# Revit family: METALFIRE_ULTIME_D_MF_WHE_2S
name_source: partatom
category: Mechanical Equipment
revit_build: Autodesk Revit 2018 (Build: 20190510_1515(x64)
units: mm (PartAtom-declared; Revit-internal decimal feet)

## family parameters
Always vertical = Yes
Cut with Voids When Loaded = No
Host = Wall
OmniClass Number = 23.75.00.00
OmniClass Title = Climate Control (HVAC)
Part Type = Normal
Room Calculation Point = Yes
Round Connector Dimension = Use Diameter
Shared = No

## types (1)
- METALFIRE_ULTIME_D_MF_WHE_2S
    BIM BADGE = https://bim.archiproducts.com
    CO EMISSION = 0.07%
    DEPTH = 401 mm
    Description = This generation of room air independent wood fireplaces with liftable door is equipped with a dynamic combustion technique that ensures optimal combustion and high efficiency.
    ENERGY EFFICIENCY CLASS = A+
    FINE DUST EMISSION = 30 mg/Nm3
    FINISHING MATERIAL = Painted steel, cast iron
    FRAME MATERIAL = Iron - Metalfire
    HEIGHT = 504 mm
    MATERIAL DESCRIPTION = Iron, galvanized steel and vermiculite plates
    Manufacturer = Metalfire
    Model = Ultime D
    NUMBER OF ELEMENTS = 47
    OUTPUT = 19.8 kW
    OVERALL DEPTH = 597 mm
    OVERALL HEIGHT = 1461 mm
    OVERALL WIDTH = 1118 mm
    PRODUCT CODE = MF 1050-50 WHE 2S V20
    PRODUCT SHEET = https://www.archiproducts.com
    SMOKE EXHAUST = Ø250 mm
    TECHNICAL SHEET = https://www.metalfire.eu
    URL = https://www.metalfire.eu
    WEIGHT = 320.00 kg
    WIDTH = 997 mm

## geometry (parser evidence)
native form markers: Sweep x6
no freeform markers — native parametric forms only
